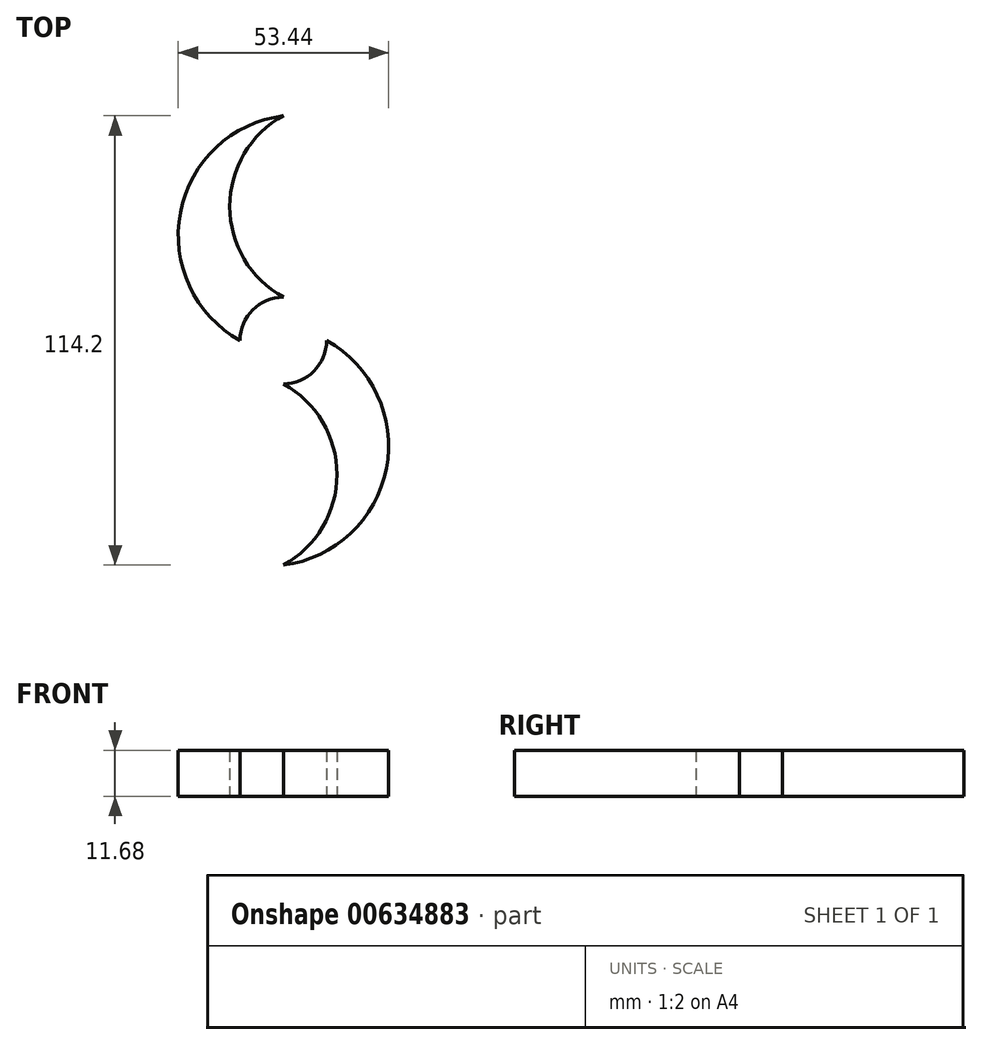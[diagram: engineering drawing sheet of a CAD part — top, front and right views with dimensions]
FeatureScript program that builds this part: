
annotation { "Feature Type Name" : "Feature", "Feature Type Description" : "" }
export const myFeature = defineFeature(function(context is Context, id is Id, definition is map)
    precondition{}
    {
        {
            var Q0;
            Q0=qCreatedBy(makeId("Top.planeOp"),FACE);
            var sketch = newSketch(context, id + "F0", { "sketchPlane" : qUnion([Q0])});
            skCircle(sketch, "E0", {"center": v(0, 0) * mm, "radius": 11 * mm});
            skPoint(sketch, "E1", {"position": v(-11, 0) * mm});
            skPoint(sketch, "E2", {"position": v(0, 11) * mm});
            skPoint(sketch, "E3", {"position": v(11, 0) * mm});
            skPoint(sketch, "E4", {"position": v(0, -11) * mm});
            skArc(sketch, "E5", {"start": v(0, 57.1) * mm, "mid": v(-13.63, 34.05) * mm, "end": v(0, 11) * mm});
            skArc(sketch, "E6", {"start": v(0, 57.1) * mm, "mid": v(-26.16, 32.53) * mm, "end": v(-11, 0) * mm});
            skPoint(sketch, "E7", {"position": v(0, -34.51) * mm});
            skPoint(sketch, "E8", {"position": v(0, 57.1) * mm});
            skPoint(sketch, "E9", {"position": v(0, 39) * mm});
            skArc(sketch, "E10.MirrorCS", {"start": v(0, -57.1) * mm, "mid": v(-26.16, -32.53) * mm, "end": v(-11, 0) * mm});
            skArc(sketch, "E11.MirrorCS", {"start": v(0, -57.1) * mm, "mid": v(-13.63, -34.05) * mm, "end": v(0, -11) * mm});
            skArc(sketch, "E12.MirrorCS", {"start": v(0, -57.1) * mm, "mid": v(26.16, -32.53) * mm, "end": v(11, 0) * mm});
            skArc(sketch, "E13.MirrorCS", {"start": v(0, -57.1) * mm, "mid": v(13.63, -34.05) * mm, "end": v(0, -11) * mm});
            skArc(sketch, "E14.MirrorCS", {"start": v(0, 57.1) * mm, "mid": v(26.16, 32.53) * mm, "end": v(11, 0) * mm});
            skArc(sketch, "E15.MirrorCS", {"start": v(0, 57.1) * mm, "mid": v(13.63, 34.05) * mm, "end": v(0, 11) * mm});
            skSolve(sketch);
        }
        {
            var Q0;
            {var subQ0=sQuery(id+"F0.wireOp",EDGE,"E5");Q0=makeQuery(id+"F0.imprint","IMPRINT",FACE,{"disambiguationData":[TD([[makeQuery(id+"F0.imprint","IMPRINT",EDGE,{"derivedFrom":subQ0}),-1.0]])]});}
            var Q1;
            {var subQ2=sQuery(id+"F0.wireOp",EDGE,"E14.MirrorCS");Q1=makeQuery(id+"F0.imprint","IMPRINT",FACE,{"disambiguationData":[TD([[makeQuery(id+"F0.imprint","IMPRINT",EDGE,{"derivedFrom":subQ2}),-1.0]])]});}
            var Q2;
            {var subQ0=sQuery(id+"F0.wireOp",EDGE,"E10.MirrorCS");Q2=makeQuery(id+"F0.imprint","IMPRINT",FACE,{"disambiguationData":[TD([[makeQuery(id+"F0.imprint","IMPRINT",EDGE,{"derivedFrom":subQ0}),-1.0]])]});}
            var Q3;
            {var subQ2=sQuery(id+"F0.wireOp",EDGE,"E12.MirrorCS");Q3=makeQuery(id+"F0.imprint","IMPRINT",FACE,{"disambiguationData":[TD([[makeQuery(id+"F0.imprint","IMPRINT",EDGE,{"derivedFrom":subQ2}),1.0]])]});}
            extrude(context, id + "F1", {"entities" : qUnion([Q0, Q1, Q2, Q3]), "depth" : 11.68 * mm, "offsetDistance" : 25.4 * mm});
        }
    });
